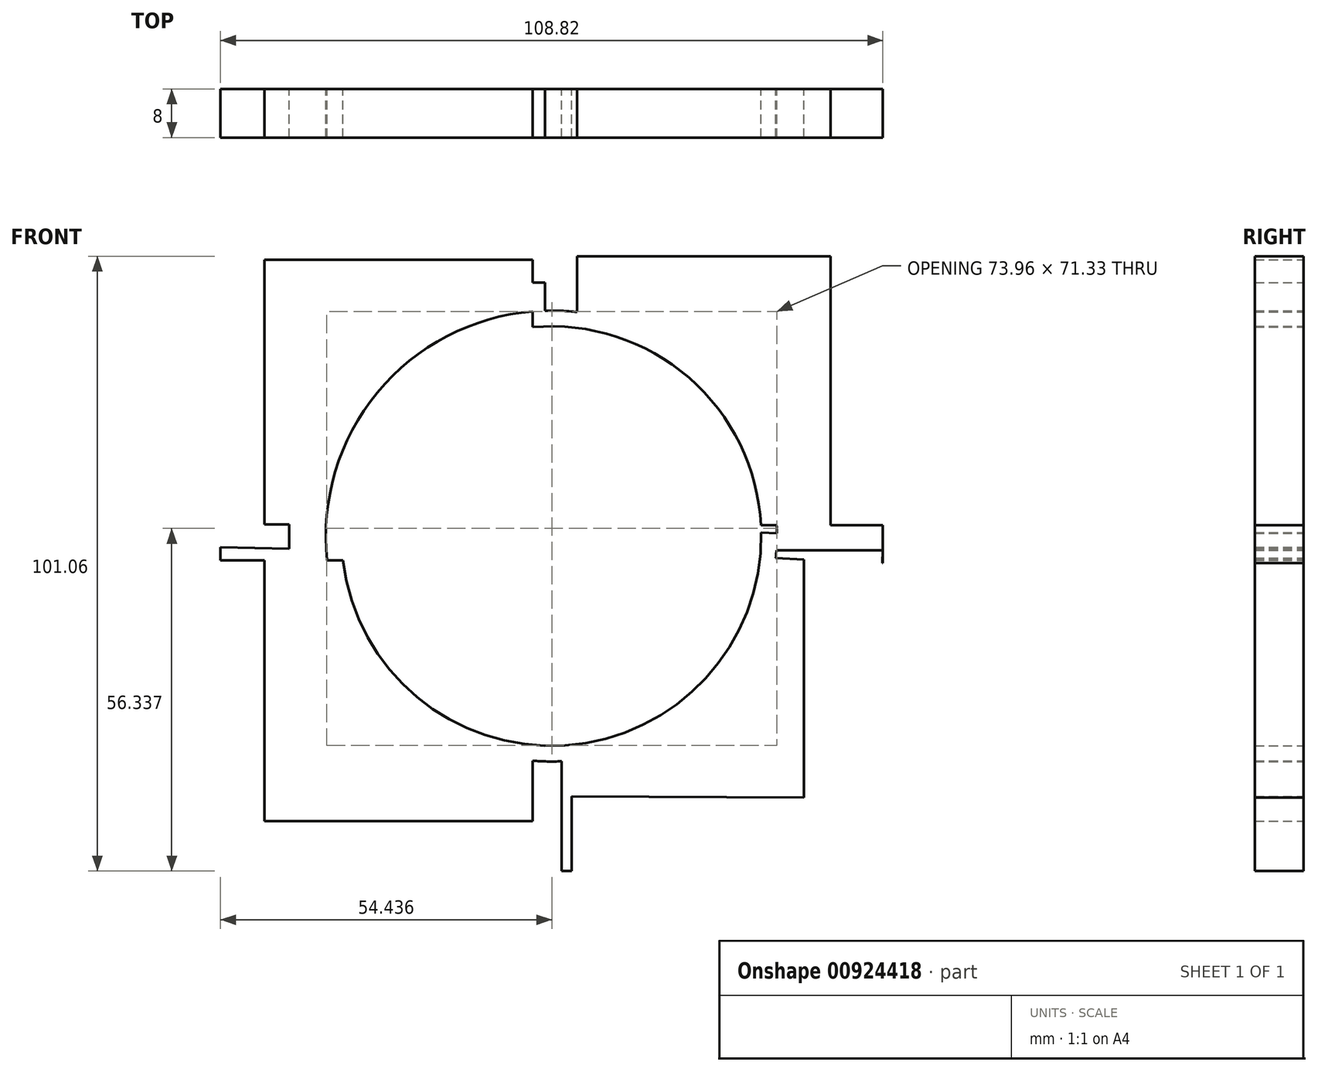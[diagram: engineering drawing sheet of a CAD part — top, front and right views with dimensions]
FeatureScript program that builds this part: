
annotation { "Feature Type Name" : "Feature", "Feature Type Description" : "" }
export const myFeature = defineFeature(function(context is Context, id is Id, definition is map)
    precondition{}
    {
        {
            var Q0;
            Q0=qCreatedBy(makeId("Front.planeOp"),FACE);
            var sketch = newSketch(context, id + "F0", { "sketchPlane" : qUnion([Q0])});
            skLineSegment(sketch, "E0", {"start": v(-47.16, -46.87) * mm, "end": v(-3.07, -46.87) * mm});
            skLineSegment(sketch, "E1", {"start": v(3.36, -46.87) * mm, "end": v(45.88, -46.87) * mm});
            skLineSegment(sketch, "E2", {"start": v(45.88, 46) * mm, "end": v(4.23, 46) * mm});
            skLineSegment(sketch, "E3", {"start": v(-47.16, 45.4) * mm, "end": v(-3.07, 45.4) * mm});
            skLineSegment(sketch, "E4", {"start": v(-3.07, 45.4) * mm, "end": v(-3.07, 31.68) * mm});
            skLineSegment(sketch, "E5", {"start": v(4.23, 46) * mm, "end": v(4.23, 29.93) * mm});
            skLineSegment(sketch, "E6", {"start": v(-3.07, 31.68) * mm, "end": v(-3.07, 28.76) * mm});
            skLineSegment(sketch, "E7", {"start": v(-3.07, 28.76) * mm, "end": v(4.23, 28.76) * mm});
            skLineSegment(sketch, "E8", {"start": v(4.23, 28.76) * mm, "end": v(4.23, 33.73) * mm});
            skLineSegment(sketch, "E9", {"start": v(-3.07, 45.4) * mm, "end": v(-3.07, 53.26) * mm});
            skLineSegment(sketch, "E10", {"start": v(4.23, 46) * mm, "end": v(4.23, 53.26) * mm});
            skLineSegment(sketch, "E11", {"start": v(-3.07, -46.87) * mm, "end": v(-3.07, -30.51) * mm});
            skLineSegment(sketch, "E12", {"start": v(-3.07, -30.51) * mm, "end": v(3.36, -30.51) * mm});
            skLineSegment(sketch, "E13", {"start": v(3.36, -31.97) * mm, "end": v(3.36, -46.87) * mm});
            skLineSegment(sketch, "E14", {"start": v(3.36, -31.97) * mm, "end": v(3.36, -30.51) * mm});
            skLineSegment(sketch, "E15", {"start": v(3.36, -46.87) * mm, "end": v(3.36, -55.07) * mm});
            skLineSegment(sketch, "E16", {"start": v(3.36, -55.07) * mm, "end": v(1.7, -55.07) * mm});
            skLineSegment(sketch, "E17", {"start": v(1.7, -55.07) * mm, "end": v(1.7, -30.51) * mm});
            skLineSegment(sketch, "E18", {"start": v(-3.07, -46.87) * mm, "end": v(-3.07, -55.07) * mm});
            skLineSegment(sketch, "E19", {"start": v(-3.07, -55.07) * mm, "end": v(-0.63, -55.07) * mm});
            skLineSegment(sketch, "E20", {"start": v(-0.63, -54.8) * mm, "end": v(-1.22, -30.51) * mm});
            skLineSegment(sketch, "E21", {"start": v(2.88, 30.26) * mm, "end": v(2.88, 53.26) * mm});
            skLineSegment(sketch, "E22", {"start": v(-1.04, 30.07) * mm, "end": v(-1.04, 53.26) * mm});
            skLineSegment(sketch, "E23", {"start": v(-43.1, 41.2) * mm, "end": v(-43.1, -42.96) * mm});
            skLineSegment(sketch, "E24", {"start": v(-43.1, -42.96) * mm, "end": v(-3.07, -42.96) * mm});
            skLineSegment(sketch, "E25", {"start": v(3.36, -42.8) * mm, "end": v(41.51, -42.96) * mm});
            skPoint(sketch, "E25.startSnap0", {"position": v(1.7, -42.8) * mm});
            skLineSegment(sketch, "E26", {"start": v(41.51, -42.96) * mm, "end": v(41.51, -3.88) * mm});
            skLineSegment(sketch, "E27", {"start": v(41.51, 1.76) * mm, "end": v(41.51, 41.22) * mm});
            skLineSegment(sketch, "E28", {"start": v(41.51, 41.22) * mm, "end": v(4.23, 41.22) * mm});
            skLineSegment(sketch, "E29", {"start": v(-1.04, 41.66) * mm, "end": v(-43.1, 41.66) * mm});
            skLineSegment(sketch, "E30", {"start": v(-43.1, 41.2) * mm, "end": v(-43.1, 41.66) * mm});
            skCircle(sketch, "E31", {"center": v(0, 0) * mm, "radius": 37.06 * mm});
            skCircle(sketch, "E32", {"center": v(0, 0) * mm, "radius": 34.47 * mm});
            skCircle(sketch, "E33", {"center": v(0, 0) * mm, "radius": 21.69 * mm});
            skCircle(sketch, "E34", {"center": v(0, 0) * mm, "radius": 10.83 * mm});
            skLineSegment(sketch, "E35", {"start": v(-30.5, 1.89) * mm, "end": v(-54.36, 1.89) * mm});
            skLineSegment(sketch, "E36", {"start": v(-54.36, 1.89) * mm, "end": v(-54.36, 0) * mm});
            skLineSegment(sketch, "E37", {"start": v(-54.22, 0.53) * mm, "end": v(-30.43, 0.53) * mm});
            skLineSegment(sketch, "E38", {"start": v(-30.43, 0.33) * mm, "end": v(-30.5, 1.89) * mm});
            skLineSegment(sketch, "E39", {"start": v(-30.43, -2.44) * mm, "end": v(-30.5, -3.99) * mm});
            skLineSegment(sketch, "E40", {"start": v(-30.5, -3.99) * mm, "end": v(-54.36, -3.99) * mm});
            skLineSegment(sketch, "E41", {"start": v(-54.36, -3.99) * mm, "end": v(-54.36, -1.8) * mm});
            skLineSegment(sketch, "E42", {"start": v(-54.36, -1.8) * mm, "end": v(-30.43, -2.44) * mm});
            skLineSegment(sketch, "E43", {"start": v(-47.16, -46.87) * mm, "end": v(-47.16, -3.99) * mm});
            skLineSegment(sketch, "E44", {"start": v(-47.16, 1.89) * mm, "end": v(-47.16, 45.4) * mm});
            skLineSegment(sketch, "E45", {"start": v(45.88, -46.87) * mm, "end": v(45.88, -3.86) * mm});
            skLineSegment(sketch, "E46", {"start": v(45.88, 0) * mm, "end": v(45.88, 46) * mm});
            skLineSegment(sketch, "E47", {"start": v(41.51, 1.76) * mm, "end": v(31.1, 1.76) * mm});
            skLineSegment(sketch, "E48", {"start": v(31.1, 1.92) * mm, "end": v(31.1, -3.28) * mm});
            skLineSegment(sketch, "E49", {"start": v(30.9, -3.28) * mm, "end": v(41.51, -3.88) * mm});
            skLineSegment(sketch, "E50", {"start": v(46.11, -4.44) * mm, "end": v(54.46, -4.44) * mm});
            skLineSegment(sketch, "E51", {"start": v(54.4, -4.63) * mm, "end": v(54.46, 0) * mm});
            skPoint(sketch, "E51.endSnap0", {"position": v(54.46, -0.9) * mm});
            skLineSegment(sketch, "E52", {"start": v(54.46, -4.44) * mm, "end": v(54.46, 1.76) * mm});
            skLineSegment(sketch, "E53", {"start": v(54.46, 1.76) * mm, "end": v(41.51, 1.76) * mm});
            skLineSegment(sketch, "E54", {"start": v(31.1, 0.65) * mm, "end": v(54.46, 0) * mm});
            skLineSegment(sketch, "E55", {"start": v(54.43, -2.31) * mm, "end": v(31.1, -2.31) * mm});
            skLineSegment(sketch, "E56", {"start": v(-1.24, 10.76) * mm, "end": v(-1.24, 25.98) * mm});
            skLineSegment(sketch, "E57", {"start": v(-1.27, 25.98) * mm, "end": v(1.02, 25.98) * mm});
            skLineSegment(sketch, "E58", {"start": v(1.02, 25.84) * mm, "end": v(1.02, 10.79) * mm});
            skLineSegment(sketch, "E59", {"start": v(10.83, 0) * mm, "end": v(26.76, 0) * mm});
            skLineSegment(sketch, "E60", {"start": v(26.76, -0.03) * mm, "end": v(26.76, -1.83) * mm});
            skLineSegment(sketch, "E61", {"start": v(26.8, -1.83) * mm, "end": v(10.68, -1.83) * mm});
            skLineSegment(sketch, "E62", {"start": v(-10.83, 0) * mm, "end": v(-26.4, 0) * mm});
            skLineSegment(sketch, "E63", {"start": v(-26.62, -0.08) * mm, "end": v(-26.62, -2.5) * mm});
            skLineSegment(sketch, "E64", {"start": v(-10.62, -2.16) * mm, "end": v(-26.62, -2.16) * mm});
            skLineSegment(sketch, "E65", {"start": v(-10.83, 0) * mm, "end": v(-22.32, 0) * mm});
            skLineSegment(sketch, "E66", {"start": v(-22.32, 0) * mm, "end": v(-25.65, 0) * mm});
            skLineSegment(sketch, "E67", {"start": v(1.22, -10.76) * mm, "end": v(1.22, -27.28) * mm});
            skLineSegment(sketch, "E68", {"start": v(1.4, -27.44) * mm, "end": v(-1.28, -27.44) * mm});
            skLineSegment(sketch, "E69", {"start": v(-1.28, -27.5) * mm, "end": v(-1.28, -10.76) * mm});
            skSolve(sketch);
        }
        {
            var Q0;
            Q0 = qSketchRegion(id + "F0", true);
            extrude(context, id + "F1", {"entities" : qUnion([Q0]), "depth" : 8 * mm, "offsetDistance" : 25.4 * mm});
        }
    });
